# Revit family: Nuaire_IfcFanType_Faith
name_source: partatom
category: Mechanical Equipment
revit_build: Autodesk Revit 2018 (Build: 20170223_1515(x64)
units: mm (PartAtom-declared; Revit-internal decimal feet)

## family parameters
Always vertical = Yes
Cut with Voids When Loaded = No
OmniClass Number = 23.75.00.00
OmniClass Title = Climate Control (HVAC)
Part Type = Normal
Room Calculation Point = No
Round Connector Dimension = Use Radius
Shared = No
Work Plane-Based = No

## types (2) — shared parameters
6 Monthly = SFG20 20-06
Annually = SFG20 20-06
Apparent Load = 12.65 VA
BMS Links = No
Battery Supply = No
CE Approval = Yes
COBie.Type = Yes
COBie.Type.Category = Pr_65_67_29_12 : Centrifugal Fans
COBie.Type.Length = 46 mm  [stored 0.150919 ft]
COBie.Type.Manufacturer = Nuaire
COBie.Type.NominalHeight = 164 mm  [stored 0.538058 ft]
COBie.Type.NominalLength = 46 mm  [stored 0.150919 ft]
COBie.Type.NominalWidth = 164 mm  [stored 0.538058 ft]
COBie.Type.WarrantyDescription = 5 years.  First year parts and labour, remaining 4 years parts only.
COBie.Type.WarrantyDurationLabor = 1
COBie.Type.WarrantyDurationParts = 5
COBie.Type.WarrantyDurationUnit = Year
COBie.Type.WarrantyGuarantorLabor = Nuaire
COBie.Type.WarrantyGuarantorParts = Nuaire
Catalogue Pages = http://nuaire.info
Classification.Uniclass.Pr.Description = Mixed flow fans
Classification.Uniclass.Pr.Number = Pr_65_67_29_52
Daily = SFG20 20-06
Environmental Product Declaration = WEEE, RoHS
Fax Number = +44(0)2920-858-222
Fire Control Panel Links = No
Frequency = 50.00 Hz
Full Load Current = 0.055 A
Height = 164 mm  [stored 0.538058 ft]
I&M Manual = http://nuaire.info
IFCExportAs = IfcFanType
IFCExportType = USERDEFINED
Length = 46 mm  [stored 0.150919 ft]
Location of Manufacturer = 51.571856, -3.232638
Maintenance Required 0 to 300hrs = http://nuaire.info
Maintenance Required 1001 to 2000hrs = http://nuaire.info
Maintenance Required 2001 to 4000hrs = http://nuaire.info
Maintenance Required 301 to 600hrs = http://nuaire.info
Maintenance Required 4001 to 8000hrs = http://nuaire.info
Maintenance Required 601 to 1000hrs = http://nuaire.info
Maintenance Required 8001 to 12000hrs = http://nuaire.info
Manufacturer = Nuaire
Manufacturer Website = http://www.nuaire.co.uk
Maximum Ambient Temperature = 40.00 °C
Monthly = SFG20 20-06
Nominal Motor Rating = 0.005 kW
Nominal Motor Speed (rpm) = 2700
Number of Connection Poles = 2
OmniClass Number = 23-33 31 19
OmniClass Title = Fans
Operation and Maintenance Manual = http://nuaire.info
Postcode = CF83 1NA
Power Source = Mains
Product Literature = http://nuaire.info
Product Range = Faith
Quarterly = SFG20 20-06
Reference Standard = BS EN 60335-2-80
Responsible Sourcing of Materials = FSC
Revit Family Last Revised = 2021-10-04T14:12:00
Spigot Diameter = 100 mm  [stored 0.328084 ft]
Spigot Radius = 50 mm  [stored 0.164042 ft]
Starting Current = 0.300 A
Supply Phase = 1
Telephone Number = +44(0)2920-858-200
URL = http://www.nuaire.co.uk
VAT Registration Number = 877308
Voltage = 230.00 V
Weatherproof or Internal Only = Internal
Weekly = SFG20 20-06
Weight = 0.60 kg
Width = 164 mm  [stored 0.538058 ft]
zero-valued in all types: COBie.Type.ReplacementCost, Life Cycle Analysis

## per-type parameters (varying)
| type | COBie.Type.Description | COBie.Type.ModelNumber | COBie.Type.ModelReference | COBie.Type.Name | Description | Model | Type Comments |
| Faith | 230v DC Continuous Mixed Flow Extract Fan | FAITH | FAITH | FAITH | 230v DC Continuous Mixed Flow Extract Fan | FAITH |  |
| Faith SELV | 24v DC Continuous Mixed Flow Extract Fan | FAITH-SELV | FAITH-SELV | FAITH-SELV | 24v DC Continuous Mixed Flow Extract Fan | FAITH-SELV | 1 |

note: [stored X ft] marks values corroborated as IEEE doubles in the binary element streams (Revit-internal decimal feet)

## geometry (parser evidence)
native form markers: Blend x8, Sweep x15
no freeform markers — native parametric forms only
